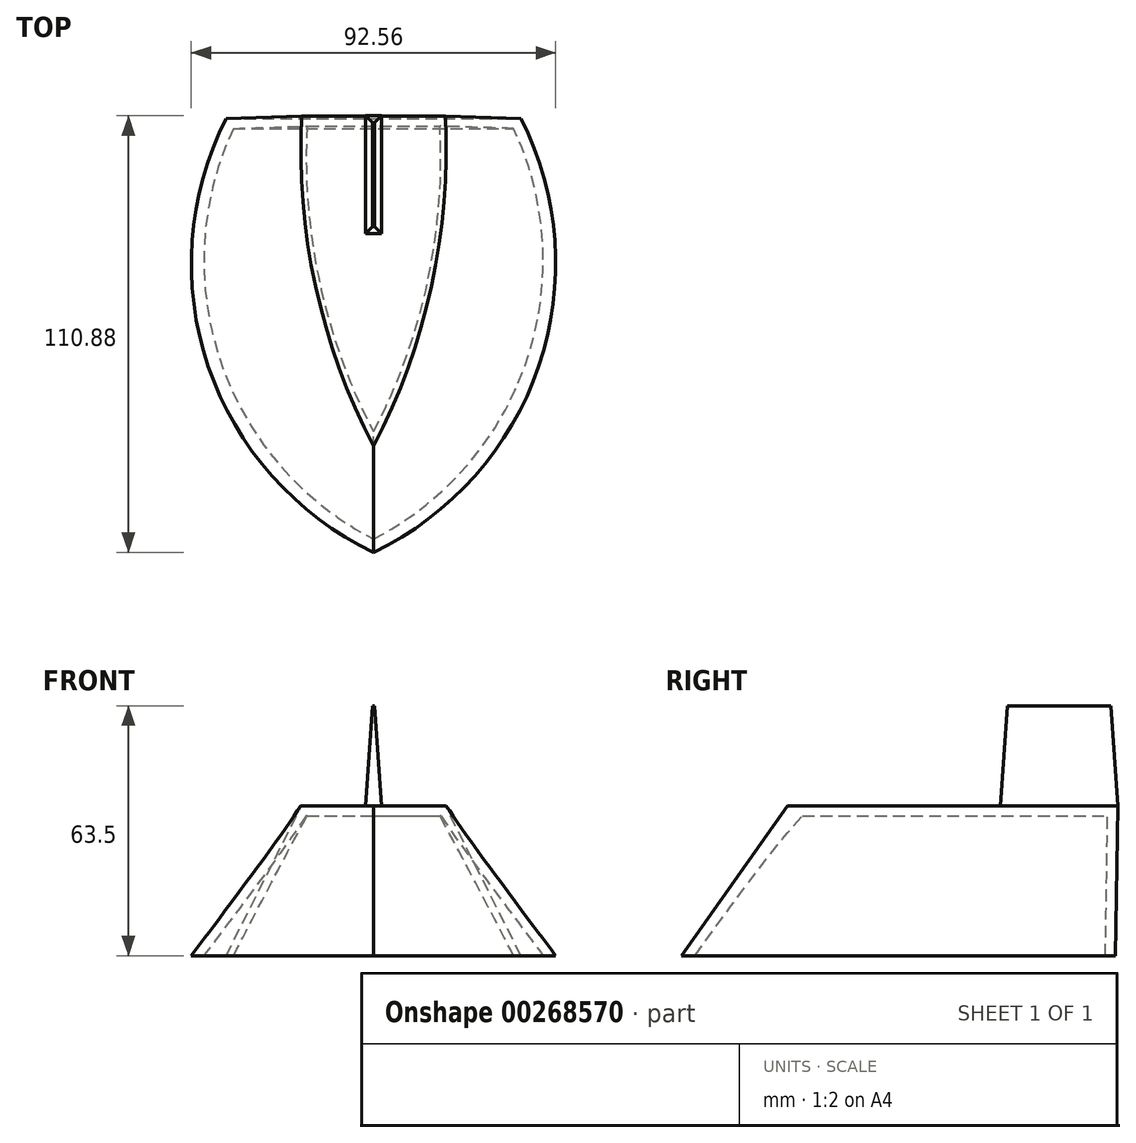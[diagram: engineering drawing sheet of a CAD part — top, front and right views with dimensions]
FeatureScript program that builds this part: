
annotation { "Feature Type Name" : "Feature", "Feature Type Description" : "" }
export const myFeature = defineFeature(function(context is Context, id is Id, definition is map)
    precondition{}
    {
        {
            var Q0;
            Q0=qCreatedBy(makeId("Top.planeOp"),FACE);
            var sketch = newSketch(context, id + "F0", { "sketchPlane" : qUnion([Q0])});
            skLineSegment(sketch, "E0", {"start": v(0, 59.9) * mm, "end": v(-37.45, 59.9) * mm});
            skArc(sketch, "E1", {"start": v(-37.45, 59.9) * mm, "mid": v(-41.96, -3.1) * mm, "end": v(0, -50.3) * mm});
            skLineSegment(sketch, "E2.MirrorCS", {"start": v(0, 59.9) * mm, "end": v(37.45, 59.9) * mm});
            skArc(sketch, "E3.MirrorCS", {"start": v(37.45, 59.9) * mm, "mid": v(41.96, -3.1) * mm, "end": v(0, -50.3) * mm});
            skSolve(sketch);
        }
        {
            var Q0;
            Q0=qCreatedBy(makeId("Top.planeOp"),FACE);
            cPlane(context, id + "F1", {"entities" : qUnion([Q0]), "cplaneType" : CPlaneType.OFFSET, "offset" : 38.1 * mm, "width" : 152.4 * mm, "height" : 152.4 * mm});
        }
        {
            var Q0;
            Q0=qCreatedBy(id+"F1.planeOp",FACE);
            var sketch = newSketch(context, id + "F2", { "sketchPlane" : qUnion([Q0])});
            skLineSegment(sketch, "E4", {"start": v(-18.26, 60.51) * mm, "end": v(0, 60.51) * mm});
            skArc(sketch, "E5", {"start": v(-18.26, 60.51) * mm, "mid": v(-14.75, 17.35) * mm, "end": v(0, -23.37) * mm});
            skLineSegment(sketch, "E6.MirrorCS", {"start": v(18.26, 60.51) * mm, "end": v(0, 60.51) * mm});
            skArc(sketch, "E7.MirrorCS", {"start": v(18.26, 60.51) * mm, "mid": v(14.75, 17.35) * mm, "end": v(0, -23.37) * mm});
            skSolve(sketch);
        }
        {
            var Q0;
            Q0=makeQuery(id+"F0.imprint","IMPRINT",FACE,{"disambiguationData":[TD([[makeQuery(id+"F0.imprint","IMPRINT",EDGE,{"derivedFrom":sQuery(id+"F0.wireOp",EDGE,"E0")}),1.0]])]});
            var Q1;
            Q1=makeQuery(id+"F2.imprint","IMPRINT",FACE,{"disambiguationData":[TD([[makeQuery(id+"F2.imprint","IMPRINT",EDGE,{"derivedFrom":sQuery(id+"F2.wireOp",EDGE,"E4")}),-1.0]])]});
            loft(context, id + "F3", {"sheetProfilesArray" : [{ "sheetProfileEntities" : qUnion([Q0]) }, { "sheetProfileEntities" : qUnion([Q1]) }]});
        }
        {
            var Q0;
            Q0=makeQuery(id+"F3.opLoft","CAP_FACE",FACE,{"disambiguationData":[OSD([makeQuery(id+"F0.imprint","IMPRINT",FACE,{"disambiguationData":[TD([[makeQuery(id+"F0.imprint","IMPRINT",EDGE,{"derivedFrom":sQuery(id+"F0.wireOp",EDGE,"E0")}),1.0]])]})])],"isStart":true});
            shell(context, id + "F4", {"entities" : qUnion([Q0]), "thickness" : 2.54 * mm});
        }
        {
            var Q0;
            Q0=qCreatedBy(id+"F1.planeOp",FACE);
            var sketch = newSketch(context, id + "F5", { "sketchPlane" : qUnion([Q0])});
            skLineSegment(sketch, "E8.bottom", {"start": v(0, 60.58) * mm, "end": v(-1.99, 60.58) * mm});
            skLineSegment(sketch, "E8.top", {"start": v(0, 30.65) * mm, "end": v(-1.99, 30.65) * mm});
            skLineSegment(sketch, "E8.right", {"start": v(-1.99, 60.58) * mm, "end": v(-1.99, 30.65) * mm});
            skLineSegment(sketch, "E9.MirrorCS", {"start": v(1.99, 60.58) * mm, "end": v(1.99, 30.65) * mm});
            skLineSegment(sketch, "E10.MirrorCS", {"start": v(0, 60.58) * mm, "end": v(1.99, 60.58) * mm});
            skLineSegment(sketch, "E11.MirrorCS", {"start": v(0, 30.65) * mm, "end": v(1.99, 30.65) * mm});
            skSolve(sketch);
        }
        {
            var Q0;
            Q0 = qSketchRegion(id + "F5", true);
            extrude(context, id + "F6", {"entities" : qUnion([Q0]), "operationType" : NewBodyOperationType.ADD, "depth" : 25.4 * mm, "hasDraft" : true, "draftAngle" : 4 * degree, "draftPullDirection" : true, "hasSecondDirectionDraft" : true, "secondDirectionDraftAngle" : 45 * degree});
        }
    });
